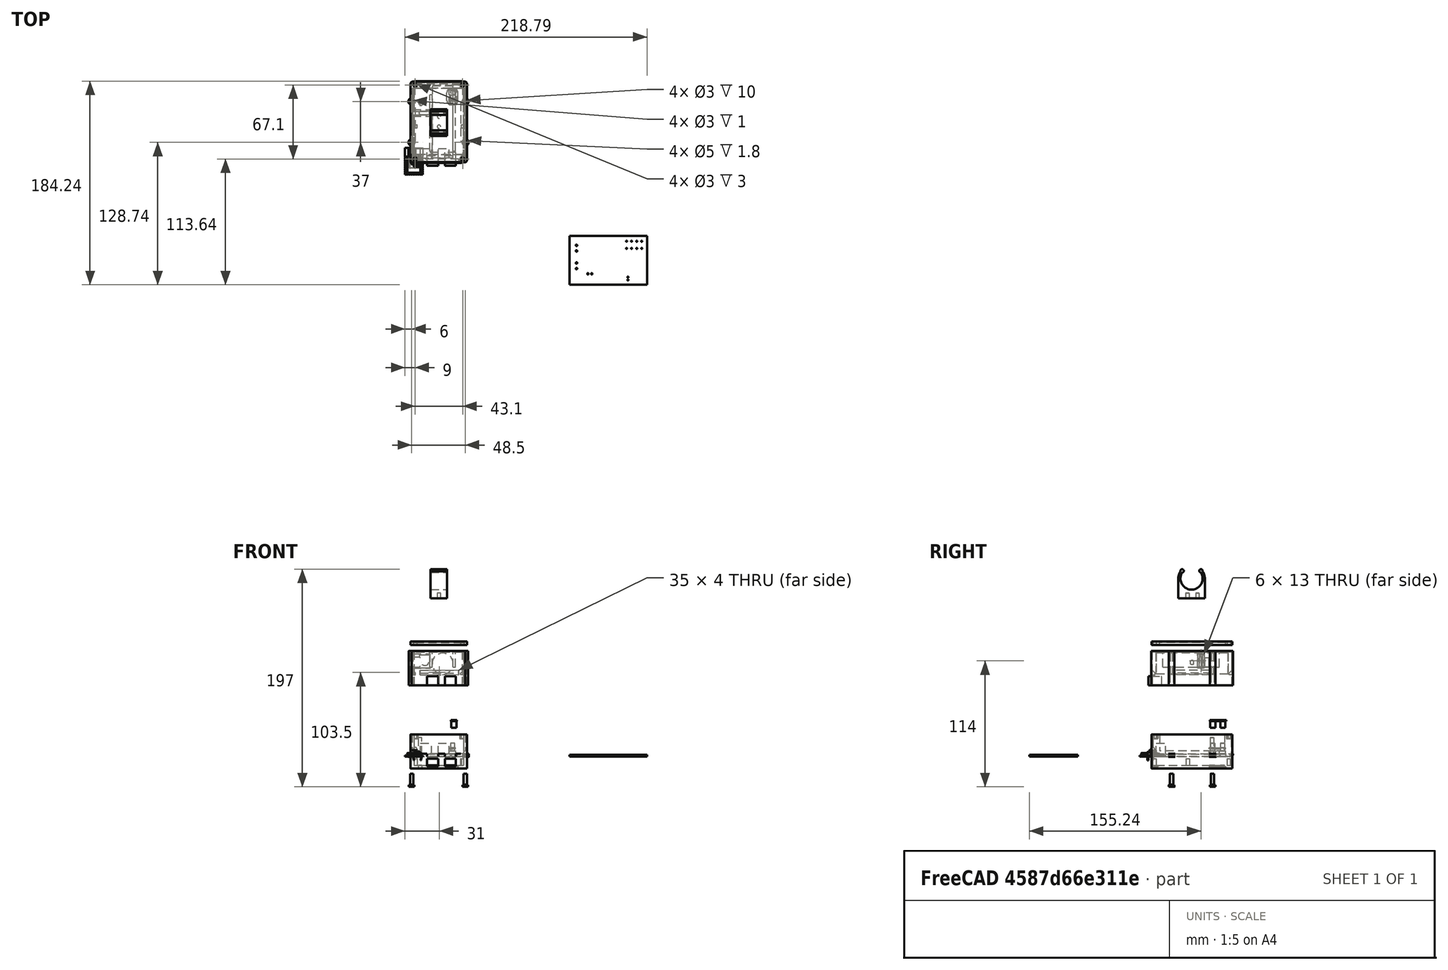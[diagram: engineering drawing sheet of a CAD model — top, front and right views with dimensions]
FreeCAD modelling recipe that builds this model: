
FCSTD DOCUMENT  (FreeCAD 0.20R29603 (Git))
Label: box_uchet_plus
License: All rights reserved
LicenseURL: http://en.wikipedia.org/wiki/All_rights_reserved
objects: Part::Box×68, Part::Cylinder×55, Part::MultiFuse×44, Part::Cut×40, Part::Feature×37, App::Part×37, Part::Fillet×31, Part::FeaturePython×16, Part::Chamfer×6, Part::Part2DObjectPython×5, Part::Extrusion×2, Part::MultiCommon×1, Part::Mirroring×1
note: 306 computed .brp shape members not serialized (recipe doc carries the construction recipe); baked Part::Feature solids carry a one-line shape summary decoded from their .brp

FEATURE [Part::Box] Box  label="Куб"
  AttacherType = Attacher::AttachEngine3D
  Height = 2
  Length = 45
  Width = 70
FEATURE [Part::Box] Box001  label="Куб001"
  AttacherType = Attacher::AttachEngine3D
  Height = 10
  Length = 10
  Placement = pos=(6,3,2) rot=(0,0,1;0rad)
  Width = 8.5
FEATURE [Part::Box] Box002  label="Куб002"
  AttacherType = Attacher::AttachEngine3D
  Height = 10
  Length = 10
  Placement = pos=(22,3,2) rot=(0,0,1;0rad)
  Width = 8.5
FEATURE [Part::Cylinder] Cylinder  label="Цилиндр"
  Angle = 360
  AttacherType = Attacher::AttachEngine3D
  FirstAngle = 0
  Height = 17
  Placement = pos=(5.5,53.5,0) rot=(0,0,1;0rad)
  Radius = 1.5
  SecondAngle = 0
FEATURE [Part::Box] Box003  label="Куб003"
  AttacherType = Attacher::AttachEngine3D
  Height = 3
  Length = 6
  Width = 6
FEATURE [Part::Cylinder] Cylinder001  label="Цилиндр001"
  Angle = 360
  AttacherType = Attacher::AttachEngine3D
  FirstAngle = 0
  Height = 10
  Placement = pos=(3,3,0) rot=(0,0,1;0rad)
  Radius = 2
  SecondAngle = 0
FEATURE [Part::MultiFuse] Fusion
  Placement = pos=(32,60,2) rot=(0,0,1;0rad)
  Shapes = -> [Cylinder001,Box003]
FEATURE [Part::Box] Box004  label="Куб004"
  AttacherType = Attacher::AttachEngine3D
  Height = 3
  Length = 6
  Width = 6
FEATURE [Part::Cylinder] Cylinder002  label="Цилиндр002"
  Angle = 360
  AttacherType = Attacher::AttachEngine3D
  FirstAngle = 0
  Height = 10
  Placement = pos=(3,3,0) rot=(0,0,1;0rad)
  Radius = 2
  SecondAngle = 0
FEATURE [Part::MultiFuse] Fusion001
  Placement = pos=(32,51,2) rot=(0,0,1;0rad)
  Shapes = -> [Cylinder002,Box004]
FEATURE [Part::Box] Box005  label="Куб005"
  AttacherType = Attacher::AttachEngine3D
  Height = 12
  Length = 45
  Placement = pos=(0,0,-4) rot=(0,0,1;0rad)
  Width = 70
FEATURE [Part::MultiFuse] Fusion002
  Shapes = -> [Fusion001,Fusion,Cylinder,Box002,Box001,Box]
FEATURE [Part::Box] Box006  label="Куб006"
  AttacherType = Attacher::AttachEngine3D
  Height = 16
  Length = 48
  Placement = pos=(-1.5,6,-21) rot=(0,0,1;0rad)
  Width = 59
FEATURE [Part::Box] Box007  label="Куб007"
  AttacherType = Attacher::AttachEngine3D
  Height = 15
  Length = 51
  Placement = pos=(-3,-1,-4) rot=(0,0,1;0rad)
  Width = 72
FEATURE [Part::Cut] Cut
  Base = -> Box007
  Tool = -> Box005
FEATURE [Part::Fillet] Fillet
  Base = -> Cut
  Edges = 1 edges r=2: [Edge11]
FEATURE [Part::Fillet] Fillet001
  Base = -> Fillet
  Edges = 1 edges r=2: [Edge13]
FEATURE [Part::Fillet] Fillet002
  Base = -> Fillet001
  Edges = 1 edges r=2: [Edge8]
FEATURE [Part::Fillet] Fillet003
  Base = -> Fillet002
  Edges = 1 edges r=2: [Edge16]
FEATURE [Part::Box] Box008  label="Куб008"
  AttacherType = Attacher::AttachEngine3D
  Height = 2
  Length = 45
  Width = 70
FEATURE [Part::Box] Box009  label="Куб009"
  AttacherType = Attacher::AttachEngine3D
  Height = 10
  Length = 10
  Placement = pos=(6,3,2) rot=(0,0,1;0rad)
  Width = 8.5
FEATURE [Part::Box] Box010  label="Куб010"
  AttacherType = Attacher::AttachEngine3D
  Height = 10
  Length = 10
  Placement = pos=(22,3,2) rot=(0,0,1;0rad)
  Width = 8.5
FEATURE [Part::Box] Box011  label="Куб011"
  AttacherType = Attacher::AttachEngine3D
  Height = 3
  Length = 6
  Width = 6
FEATURE [Part::Box] Box012  label="Куб012"
  AttacherType = Attacher::AttachEngine3D
  Height = 3
  Length = 6
  Width = 6
FEATURE [Part::Cylinder] Cylinder003  label="Цилиндр003"
  Angle = 360
  AttacherType = Attacher::AttachEngine3D
  FirstAngle = 0
  Height = 17
  Placement = pos=(5.5,53.5,0) rot=(0,0,1;0rad)
  Radius = 1.5
  SecondAngle = 0
FEATURE [Part::Cylinder] Cylinder004  label="Цилиндр004"
  Angle = 360
  AttacherType = Attacher::AttachEngine3D
  FirstAngle = 0
  Height = 10
  Placement = pos=(3,3,0) rot=(0,0,1;0rad)
  Radius = 2
  SecondAngle = 0
FEATURE [Part::Cylinder] Cylinder005  label="Цилиндр005"
  Angle = 360
  AttacherType = Attacher::AttachEngine3D
  FirstAngle = 0
  Height = 10
  Placement = pos=(3,3,0) rot=(0,0,1;0rad)
  Radius = 2
  SecondAngle = 0
FEATURE [Part::MultiFuse] Fusion003
  Placement = pos=(32,60,2) rot=(0,0,1;0rad)
  Shapes = -> [Cylinder004,Box011]
FEATURE [Part::MultiFuse] Fusion004
  Placement = pos=(32,51,2) rot=(0,0,1;0rad)
  Shapes = -> [Cylinder005,Box012]
FEATURE [Part::MultiFuse] Fusion005
  Shapes = -> [Fusion004,Fusion003,Cylinder003,Box010,Box009,Box008]
FEATURE [Part::Cut] Cut001
  Base = -> Fillet003
  Tool = -> Fusion002
FEATURE [Part::Box] Box013  label="Куб013"
  AttacherType = Attacher::AttachEngine3D
  Height = 7
  Length = 10
  Placement = pos=(6,-4,2) rot=(0,0,1;0rad)
  Width = 9
FEATURE [Part::Box] Box014  label="Куб014"
  AttacherType = Attacher::AttachEngine3D
  Height = 7
  Length = 10
  Placement = pos=(22,-3,2) rot=(0,0,1;0rad)
  Width = 8
FEATURE [Part::Cut] Cut002
  Base = -> Cut001
  Tool = -> Box013
FEATURE [Part::Cut] Cut003
  Base = -> Cut002
  Tool = -> Box014
FEATURE [Part::Box] Box015  label="Куб015"
  AttacherType = Attacher::AttachEngine3D
  Height = 10
  Length = 19
  Placement = pos=(30,49,9.5) rot=(0,0,1;0rad)
  Width = 19
FEATURE [Part::Fillet] Fillet004
  Base = -> Box015
  Edges = 2 edges r=3: [Edge1,Edge3]
FEATURE [Part::Cut] Cut004
  Base = -> Cut003
  Tool = -> Fillet004
FEATURE [Part::Fillet] Fillet005
  Base = -> Cut004
  Edges = 1 edges r=3: [Edge29]
FEATURE [Part::Fillet] Fillet006
  Base = -> Fillet005
  Edges = 1 edges r=0.5: [Edge35]
FEATURE [Part::Box] Box016  label="Куб016"
  AttacherType = Attacher::AttachEngine3D
  Height = 9
  Length = 3
  Placement = pos=(0,0,2) rot=(0,0,1;0rad)
  Width = 3
FEATURE [Part::Box] Box017  label="Куб017"
  AttacherType = Attacher::AttachEngine3D
  Height = 9
  Length = 3
  Placement = pos=(0,30,2) rot=(0,0,1;0rad)
  Width = 3
FEATURE [Part::Box] Box018  label="Куб018"
  AttacherType = Attacher::AttachEngine3D
  Height = 9
  Length = 3
  Placement = pos=(0,67,2) rot=(0,0,1;0rad)
  Width = 3
FEATURE [Part::Box] Box019  label="Куб019"
  AttacherType = Attacher::AttachEngine3D
  Height = 9
  Length = 3
  Placement = pos=(27,57,2) rot=(0,0,1;0rad)
  Width = 3
FEATURE [Part::Box] Box020  label="Куб020"
  AttacherType = Attacher::AttachEngine3D
  Height = 9
  Length = 3
  Placement = pos=(45,31,2) rot=(0,0,1;0rad)
  Width = 3
FEATURE [Part::Box] Box021  label="Куб021"
  AttacherType = Attacher::AttachEngine3D
  Height = 9
  Length = 3
  Placement = pos=(42,0,2) rot=(0,0,1;0rad)
  Width = 3
FEATURE [Part::Box] Box022  label="Куб022"
  AttacherType = Attacher::AttachEngine3D
  Height = 7
  Length = 3
  Placement = pos=(42,67,2) rot=(0,0,1;0rad)
  Width = 3
FEATURE [Part::MultiFuse] Fusion006
  Shapes = -> [Box021,Box022,Box020,Box018,Box019,Box017,Box016,Fillet006]
FEATURE [Part::Box] Box025  label="Куб025"
  AttacherType = Attacher::AttachEngine3D
  Height = 16
  Length = 45
  Placement = pos=(0,0,-20) rot=(0,0,1;0rad)
  Width = 71
FEATURE [Part::Box] Box026  label="Куб026"
  AttacherType = Attacher::AttachEngine3D
  Height = 16
  Length = 51
  Placement = pos=(-3,-1,-20) rot=(0,0,1;0rad)
  Width = 73
FEATURE [Part::Cut] Cut005
  Base = -> Box026
  Tool = -> Box025
FEATURE [Part::Fillet] Fillet007
  Base = -> Cut005
  Edges = 4 edges r=2: [Edge1,Edge3,Edge6,Edge15]
FEATURE [Part::Cut] Cut006
  Base = -> Fillet007
  Tool = -> Box006
FEATURE [Part::MultiFuse] Fusion007
  Shapes = -> [Cut006,Fusion006]
FEATURE [Part::FeaturePython] Tube  # WARN: FeaturePython — macro-defined, semantics opaque (R4)
  AttacherType = Attacher::AttachEngine3D
  Height = 4
  InnerRadius = 1.4
  OuterRadius = 2.5
  Placement = pos=(1,2,-20) rot=(0,0,1;0rad)
FEATURE [Part::FeaturePython] Tube001  # WARN: FeaturePython — macro-defined, semantics opaque (R4)
  AttacherType = Attacher::AttachEngine3D
  Height = 4
  InnerRadius = 1.4
  OuterRadius = 2.5
  Placement = pos=(44,2,-20) rot=(0,0,1;0rad)
FEATURE [Part::FeaturePython] Tube002  # WARN: FeaturePython — macro-defined, semantics opaque (R4)
  AttacherType = Attacher::AttachEngine3D
  Height = 4
  InnerRadius = 1.4
  OuterRadius = 2.5
  Placement = pos=(44.1,69.1,-20) rot=(0,0,1;0rad)
FEATURE [Part::FeaturePython] Tube003  # WARN: FeaturePython — macro-defined, semantics opaque (R4)
  AttacherType = Attacher::AttachEngine3D
  Height = 4
  InnerRadius = 1.4
  OuterRadius = 2.5
  Placement = pos=(1.1,69.1,-20) rot=(0,0,1;0rad)
FEATURE [Part::MultiFuse] Fusion008
  Shapes = -> [Fusion007,Tube,Tube001,Tube002,Tube003]
FEATURE [Part::Part2DObjectPython] ShapeString  # Draft 2D object (typed FeaturePython)
  FontFile = <userpath>/Downloads/Roboto/Roboto-Bold.ttf
  MakeFace = true
  Placement = pos=(-54.85,40.61,0) rot=(0,0,1;0rad)
  Size = 8
  String = 1
  Tracking = 0
FEATURE [Part::Part2DObjectPython] ShapeString001  # Draft 2D object (typed FeaturePython)
  FontFile = <userpath>/Downloads/Roboto/Roboto-Bold.ttf
  MakeFace = true
  Placement = pos=(-54.85,40.61,0) rot=(0,0,1;0rad)
  Size = 8
  String = 2
  Tracking = 0
FEATURE [Part::Extrusion] Extrude001
  Base = -> ShapeString001
  Dir = (0,0,1)
  DirMode = 2
  FaceMakerClass = Part::FaceMakerBullseye
  LengthFwd = 5
  LengthRev = 0
  Placement = pos=(55,69,9) rot=(0,0,1;1.5708rad)
  Solid = false
  Symmetric = false
FEATURE [Part::Part2DObjectPython] ShapeString002  # Draft 2D object (typed FeaturePython)
  FontFile = <userpath>/Downloads/Roboto/Roboto-Bold.ttf
  MakeFace = true
  Placement = pos=(-54.85,40.61,0) rot=(0,0,1;0rad)
  Size = 8
  String = 1
  Tracking = 0
FEATURE [Part::Extrusion] Extrude002
  Base = -> ShapeString002
  Dir = (0,0,1)
  DirMode = 2
  FaceMakerClass = Part::FaceMakerBullseye
  LengthFwd = 5
  LengthRev = 0
  Placement = pos=(71,69,9) rot=(0,0,1;1.5708rad)
  Solid = false
  Symmetric = false
FEATURE [Part::Cut] Cut007
  Base = -> Fusion008
  Tool = -> Extrude001
FEATURE [Part::Cut] Cut008
  Base = -> Cut007
  Tool = -> Extrude002
FEATURE [Part::Box] Box027  label="Куб027"
  AttacherType = Attacher::AttachEngine3D
  Height = 3
  Length = 51
  Placement = pos=(-3,-1,-23) rot=(0,0,1;0rad)
  Width = 73
FEATURE [Part::Fillet] Fillet008
  Base = -> Box027
  Edges = 4 edges r=2: [Edge1,Edge3,Edge5,Edge7]
FEATURE [Part::Box] Box028  label="Куб028"
  AttacherType = Attacher::AttachEngine3D
  Height = 2
  Length = 45
  Width = 70
FEATURE [Part::Box] Box031  label="Куб031"
  AttacherType = Attacher::AttachEngine3D
  Height = 3
  Length = 6
  Width = 6
FEATURE [Part::Box] Box032  label="Куб032"
  AttacherType = Attacher::AttachEngine3D
  Height = 3
  Length = 6
  Width = 6
FEATURE [Part::Box] Box033  label="Куб033"
  AttacherType = Attacher::AttachEngine3D
  Height = 12
  Length = 45
  Placement = pos=(0,0,-4) rot=(0,0,1;0rad)
  Width = 71
FEATURE [Part::Box] Box034  label="Куб034"
  AttacherType = Attacher::AttachEngine3D
  Height = 16
  Length = 48
  Placement = pos=(-1.5,6,-21) rot=(0,0,1;0rad)
  Width = 59
FEATURE [Part::Box] Box035  label="Куб035"
  AttacherType = Attacher::AttachEngine3D
  Height = 15
  Length = 51
  Placement = pos=(-3,-1,-4) rot=(0,0,1;0rad)
  Width = 73
FEATURE [Part::Box] Box037  label="Куб037"
  AttacherType = Attacher::AttachEngine3D
  Height = 7
  Length = 10
  Placement = pos=(28,-3,2) rot=(0,0,1;0rad)
  Width = 8
FEATURE [Part::Box] Box039  label="Куб039"
  AttacherType = Attacher::AttachEngine3D
  Height = 6
  Length = 3
  Placement = pos=(0,0,2) rot=(0,0,1;0rad)
  Width = 3
FEATURE [Part::Box] Box040  label="Куб040"
  AttacherType = Attacher::AttachEngine3D
  Height = 6
  Length = 3
  Placement = pos=(0,30,2) rot=(0,0,1;0rad)
  Width = 3
FEATURE [Part::Box] Box041  label="Куб041"
  AttacherType = Attacher::AttachEngine3D
  Height = 6
  Length = 3
  Placement = pos=(0,67,2) rot=(0,0,1;0rad)
  Width = 3
FEATURE [Part::Box] Box043  label="Куб043"
  AttacherType = Attacher::AttachEngine3D
  Height = 6
  Length = 3
  Placement = pos=(43,30,2) rot=(0,0,1;0rad)
  Width = 3
FEATURE [Part::Box] Box044  label="Куб044"
  AttacherType = Attacher::AttachEngine3D
  Height = 6
  Length = 3
  Placement = pos=(42,0,2) rot=(0,0,1;0rad)
  Width = 3
FEATURE [Part::Box] Box045  label="Куб045"
  AttacherType = Attacher::AttachEngine3D
  Height = 6
  Length = 3
  Placement = pos=(42,67,2) rot=(0,0,1;0rad)
  Width = 3
FEATURE [Part::Box] Box046  label="Куб046"
  AttacherType = Attacher::AttachEngine3D
  Height = 16
  Length = 45
  Placement = pos=(0,0,-20) rot=(0,0,1;0rad)
  Width = 71
FEATURE [Part::Box] Box047  label="Куб047"
  AttacherType = Attacher::AttachEngine3D
  Height = 16
  Length = 51
  Placement = pos=(-3,-1,-20) rot=(0,0,1;0rad)
  Width = 73
FEATURE [Part::Cut] Cut009
  Base = -> Box035
  Tool = -> Box033
FEATURE [Part::Cut] Cut014
  Base = -> Box047
  Tool = -> Box046
FEATURE [Part::Cylinder] Cylinder006  label="Цилиндр006"
  Angle = 360
  AttacherType = Attacher::AttachEngine3D
  FirstAngle = 0
  Height = 17
  Placement = pos=(5.7,52.7,0) rot=(0,0,1;0rad)
  Radius = 1.5
  SecondAngle = 0
FEATURE [Part::Cylinder] Cylinder007  label="Цилиндр007"
  Angle = 360
  AttacherType = Attacher::AttachEngine3D
  FirstAngle = 0
  Height = 10
  Placement = pos=(3,3,0) rot=(0,0,1;0rad)
  Radius = 2
  SecondAngle = 0
FEATURE [Part::Cylinder] Cylinder008  label="Цилиндр008"
  Angle = 360
  AttacherType = Attacher::AttachEngine3D
  FirstAngle = 0
  Height = 10
  Placement = pos=(3,3,0) rot=(0,0,1;0rad)
  Radius = 2
  SecondAngle = 0
FEATURE [Part::Fillet] Fillet009
  Base = -> Cut009
  Edges = 1 edges r=2: [Edge11]
FEATURE [Part::Fillet] Fillet010
  Base = -> Fillet009
  Edges = 1 edges r=2: [Edge13]
FEATURE [Part::Fillet] Fillet011
  Base = -> Fillet010
  Edges = 1 edges r=2: [Edge8]
FEATURE [Part::Fillet] Fillet012
  Base = -> Fillet011
  Edges = 1 edges r=2: [Edge16]
FEATURE [Part::Fillet] Fillet016
  Base = -> Cut014
  Edges = 4 edges r=2: [Edge1,Edge3,Edge6,Edge15]
FEATURE [Part::Cut] Cut015
  Base = -> Fillet016
  Tool = -> Box034
FEATURE [Part::MultiFuse] Fusion009
  Placement = pos=(32,60,2) rot=(0,0,1;0rad)
  Shapes = -> [Cylinder007,Box031]
FEATURE [Part::MultiFuse] Fusion010
  Placement = pos=(32,51,2) rot=(0,0,1;0rad)
  Shapes = -> [Cylinder008,Box032]
FEATURE [Part::MultiFuse] Fusion011
  Shapes = -> [Fusion010,Fusion009,Cylinder006,Box028]
FEATURE [Part::Cut] Cut010
  Base = -> Fillet012
  Tool = -> Fusion011
FEATURE [Part::MultiFuse] Fusion012
  Shapes = -> [Box044,Box045,Box043,Box041,Box040,Box039]
FEATURE [Part::MultiFuse] Fusion013
  Shapes = -> [Cut015,Fusion012]
FEATURE [Part::Part2DObjectPython] ShapeString003  # Draft 2D object (typed FeaturePython)
  FontFile = <userpath>/Downloads/Roboto/Roboto-Bold.ttf
  MakeFace = true
  Placement = pos=(-54.85,40.61,0) rot=(0,0,1;0rad)
  Size = 8
  String = 2
  Tracking = 0
FEATURE [Part::Part2DObjectPython] ShapeString004  # Draft 2D object (typed FeaturePython)
  FontFile = <userpath>/Downloads/Roboto/Roboto-Bold.ttf
  MakeFace = true
  Placement = pos=(-54.85,40.61,0) rot=(0,0,1;0rad)
  Size = 8
  String = 1
  Tracking = 0
FEATURE [Part::FeaturePython] Tube004  # WARN: FeaturePython — macro-defined, semantics opaque (R4)
  AttacherType = Attacher::AttachEngine3D
  Height = 4
  InnerRadius = 1.4
  OuterRadius = 2.5
  Placement = pos=(1,2,-20) rot=(0,0,1;0rad)
FEATURE [Part::FeaturePython] Tube005  # WARN: FeaturePython — macro-defined, semantics opaque (R4)
  AttacherType = Attacher::AttachEngine3D
  Height = 4
  InnerRadius = 1.4
  OuterRadius = 2.5
  Placement = pos=(44,2,-20) rot=(0,0,1;0rad)
FEATURE [Part::FeaturePython] Tube006  # WARN: FeaturePython — macro-defined, semantics opaque (R4)
  AttacherType = Attacher::AttachEngine3D
  Height = 4
  InnerRadius = 1.4
  OuterRadius = 2.5
  Placement = pos=(44,69,-20) rot=(0,0,1;0rad)
FEATURE [Part::FeaturePython] Tube007  # WARN: FeaturePython — macro-defined, semantics opaque (R4)
  AttacherType = Attacher::AttachEngine3D
  Height = 4
  InnerRadius = 1.4
  OuterRadius = 2.5
  Placement = pos=(1,69,-20) rot=(0,0,1;0rad)
FEATURE [Part::Cut] Cut018
  Base = -> Fillet008
  Tool = -> Cut008
FEATURE [Part::Cylinder] Cylinder009  label="Цилиндр009"
  Angle = 360
  AttacherType = Attacher::AttachEngine3D
  FirstAngle = 0
  Height = 10
  Placement = pos=(1,2,-24) rot=(0,0,1;0rad)
  Radius = 1.5
  SecondAngle = 0
FEATURE [Part::Cylinder] Cylinder010  label="Цилиндр010"
  Angle = 360
  AttacherType = Attacher::AttachEngine3D
  FirstAngle = 0
  Height = 10
  Placement = pos=(1.1,69.1,-26) rot=(0,0,1;0rad)
  Radius = 1.5
  SecondAngle = 0
FEATURE [Part::Cylinder] Cylinder011  label="Цилиндр011"
  Angle = 360
  AttacherType = Attacher::AttachEngine3D
  FirstAngle = 0
  Height = 10
  Placement = pos=(44.1,69.1,-26) rot=(0,0,1;0rad)
  Radius = 1.5
  SecondAngle = 0
FEATURE [Part::Cylinder] Cylinder012  label="Цилиндр012"
  Angle = 360
  AttacherType = Attacher::AttachEngine3D
  FirstAngle = 0
  Height = 10
  Placement = pos=(44,2,-24) rot=(0,0,1;0rad)
  Radius = 1.5
  SecondAngle = 0
FEATURE [Part::Cut] Cut019
  Base = -> Cut018
  Tool = -> Cylinder009
FEATURE [Part::Cut] Cut020
  Base = -> Cut019
  Tool = -> Cylinder012
FEATURE [Part::Cut] Cut021
  Base = -> Cut020
  Tool = -> Cylinder011
FEATURE [Part::Cut] Cut022
  Base = -> Cut021
  Tool = -> Cylinder010
FEATURE [Part::Cylinder] Cylinder013  label="Цилиндр013"
  Angle = 360
  AttacherType = Attacher::AttachEngine3D
  FirstAngle = 0
  Height = 15
  Radius = 10
  SecondAngle = 0
FEATURE [Part::Box] Box048  label="Куб048"
  AttacherType = Attacher::AttachEngine3D
  Height = 15
  Length = 24
  Placement = pos=(-12,-7,0) rot=(0,0,1;0rad)
  Width = 25
FEATURE [Part::Cut] Cut023
  Base = -> Box048
  Tool = -> Cylinder013
FEATURE [Part::Cylinder] Cylinder014  label="Цилиндр014"
  Angle = 360
  AttacherType = Attacher::AttachEngine3D
  FirstAngle = 0
  Height = 15
  Radius = 12
  SecondAngle = 0
FEATURE [Part::Box] Box049  label="Куб049"
  AttacherType = Attacher::AttachEngine3D
  Height = 15
  Length = 24
  Placement = pos=(-12,0,0) rot=(0,0,1;0rad)
  Width = 18
FEATURE [Part::Cylinder] Cylinder015  label="Цилиндр015"
  Angle = 360
  AttacherType = Attacher::AttachEngine3D
  FirstAngle = 0
  Height = 15
  Radius = 10
  SecondAngle = 0
FEATURE [Part::Cut] Cut024
  Base = -> Box049
  Tool = -> Cylinder015
FEATURE [Part::MultiCommon] Common
  Shapes = -> [Cut023,Cylinder014]
FEATURE [Part::Cylinder] Cylinder016  label="Цилиндр016"
  Angle = 360
  AttacherType = Attacher::AttachEngine3D
  FirstAngle = 0
  Height = 15
  Placement = pos=(-8.5,-7,0) rot=(0,0,1;0rad)
  Radius = 1.5
  SecondAngle = 0
FEATURE [Part::Cylinder] Cylinder017  label="Цилиндр017"
  Angle = 360
  AttacherType = Attacher::AttachEngine3D
  FirstAngle = 0
  Height = 15
  Placement = pos=(8.5,-7,0) rot=(0,0,1;0rad)
  Radius = 1.5
  SecondAngle = 0
FEATURE [Part::MultiFuse] Fusion015
  Placement = pos=(30,35,113) rot=(0.57735,0.57735,-0.57735;4.18879rad)
  Shapes = -> [Cut024,Common,Cylinder016,Cylinder017]
FEATURE [Part::Box] Box050  label="Куб050"
  AttacherType = Attacher::AttachEngine3D
  Height = 16
  Length = 48
  Placement = pos=(-1.5,6,-21) rot=(0,0,1;0rad)
  Width = 60
FEATURE [Part::Fillet] Fillet017
  Base = -> Box050
  Edges = 2 edges r=3: [Edge4,Edge8]
  Placement = pos=(0,-1,-1) rot=(0,0,1;0rad)
FEATURE [Part::Cylinder] Cylinder018  label="Цилиндр018"
  Angle = 360
  AttacherType = Attacher::AttachEngine3D
  FirstAngle = 0
  Height = 4
  Placement = pos=(35,63,7) rot=(0,0,1;0rad)
  Radius = 1.8
  SecondAngle = 0
FEATURE [Part::Cylinder] Cylinder019  label="Цилиндр019"
  Angle = 360
  AttacherType = Attacher::AttachEngine3D
  FirstAngle = 0
  Height = 4
  Placement = pos=(35,54,7) rot=(0,0,1;0rad)
  Radius = 1.8
  SecondAngle = 0
FEATURE [Part::Box] Box051  label="Куб051"
  AttacherType = Attacher::AttachEngine3D
  Height = 1
  Length = 5
  Placement = pos=(32.5,51,6) rot=(0,0,1;0rad)
  Width = 15
FEATURE [Part::Fillet] Fillet018
  Base = -> Box051
  Edges = 4 edges r=2: [Edge1,Edge3,Edge5,Edge7]
FEATURE [Part::MultiFuse] Fusion017
  Placement = pos=(0,0,1) rot=(0,0,1;0rad)
  Shapes = -> [Cylinder018,Cylinder019,Fillet018]
FEATURE [Part::Cut] Cut026
  Base = -> Cut022
  Placement = pos=(0,71,81) rot=(1,0,0;3.14159rad)
  Tool = -> Fillet017
FEATURE [Part::Box] Box036  label="Куб036"
  AttacherType = Attacher::AttachEngine3D
  Height = 7
  Length = 10
  Placement = pos=(12,-4,2) rot=(0,0,1;0rad)
  Width = 9
FEATURE [Part::Cut] Cut027
  Base = -> Cut010
  Tool = -> Box037
FEATURE [Part::Cut] Cut028
  Base = -> Cut027
  Tool = -> Box036
FEATURE [Part::Box] Box052  label="Куб052"
  AttacherType = Attacher::AttachEngine3D
  Height = 10
  Length = 10
  Placement = pos=(29.8,51,9) rot=(0,0,1;0rad)
  Width = 15
FEATURE [Part::Fillet] Fillet019
  Base = -> Box052
  Edges = 4 edges r=4: [Edge1,Edge3,Edge5,Edge7]
FEATURE [Part::Cut] Cut029
  Base = -> Cut028
  Tool = -> Fillet019
FEATURE [Part::MultiFuse] Fusion018
  Shapes = -> [Fusion013,Tube004,Tube005,Tube006,Tube007]
FEATURE [Part::MultiFuse] Fusion019
  Shapes = -> [Fusion018,Cut029]
FEATURE [Part::Mirroring] Part__Mirroring  label="Fusion019 (Mirror #1)"
  Base = (0,0,0)
  Normal = (0,0,1)
  Source = -> Fusion019
FEATURE [Part::Cylinder] Cylinder020  label="Цилиндр020"
  Angle = 360
  AttacherType = Attacher::AttachEngine3D
  FirstAngle = 0
  Height = 65
  Placement = pos=(26,3,84) rot=(-1,0,0;1.5708rad)
  Radius = 9.5
  SecondAngle = 0
FEATURE [Part::Box] Box053  label="Куб053"
  AttacherType = Attacher::AttachEngine3D
  Height = 8
  Length = 10
  Placement = pos=(12,-4,64.5) rot=(0,0,1;0rad)
  Width = 12
FEATURE [Part::Box] Box054  label="Куб054"
  AttacherType = Attacher::AttachEngine3D
  Height = 8
  Length = 10
  Placement = pos=(28,-4,64.5) rot=(0,0,1;0rad)
  Width = 12
FEATURE [Part::Box] Box055  label="Куб055"
  AttacherType = Attacher::AttachEngine3D
  Height = 30
  Length = 46.5
  Placement = pos=(-1,-0.5,64.5) rot=(0,0,1;0rad)
  Width = 72
FEATURE [Part::Box] Box056  label="Куб056"
  AttacherType = Attacher::AttachEngine3D
  Height = 31
  Length = 48.5
  Placement = pos=(-2,-1.5,64.5) rot=(0,0,1;0rad)
  Width = 74
FEATURE [Part::Cut] Cut030
  Base = -> Box056
  Tool = -> Box055
FEATURE [Part::Fillet] Fillet020
  Base = -> Cut030
  Edges = 1 edges r=3: [Edge17]
FEATURE [Part::Fillet] Fillet021
  Base = -> Fillet020
  Edges = 1 edges r=3: [Edge18]
FEATURE [Part::Fillet] Fillet022
  Base = -> Fillet021
  Edges = 1 edges r=3: [Edge17]
FEATURE [Part::Fillet] Fillet023
  Base = -> Fillet022
  Edges = 1 edges r=3: [Edge20]
FEATURE [Part::Fillet] Fillet024
  Base = -> Fillet023
  Edges = 1 edges r=4: [Edge29]
FEATURE [Part::Fillet] Fillet025
  Base = -> Fillet024
  Edges = 1 edges r=4: [Edge16]
FEATURE [Part::Fillet] Fillet026
  Base = -> Fillet025
  Edges = 1 edges r=4: [Edge23]
FEATURE [Part::Fillet] Fillet027
  Base = -> Fillet026
  Edges = 1 edges r=4: [Edge17]
FEATURE [Part::Box] Box057  label="Куб057"
  AttacherType = Attacher::AttachEngine3D
  Height = 8
  Length = 10
  Placement = pos=(12,-4,64.5) rot=(0,0,1;0rad)
  Width = 12
FEATURE [Part::Box] Box058  label="Куб058"
  AttacherType = Attacher::AttachEngine3D
  Height = 8
  Length = 10
  Placement = pos=(28,-4,64.5) rot=(0,0,1;0rad)
  Width = 12
FEATURE [Part::Cut] Cut031
  Base = -> Fillet027
  Tool = -> Box057
FEATURE [Part::Cut] Cut032
  Base = -> Cut031
  Tool = -> Box058
FEATURE [Part::Box] Box059  label="Куб059"
  AttacherType = Attacher::AttachEngine3D
  Height = 4
  Length = 3
  Width = 35
FEATURE [Part::Chamfer] Chamfer
  Base = -> Box059
  Edges = 1 edges r=2.5: [Edge6]
  Placement = pos=(-1.5,18,74) rot=(0,0,1;0rad)
FEATURE [Part::Box] Box060  label="Куб060"
  AttacherType = Attacher::AttachEngine3D
  Height = 4
  Length = 3
  Width = 35
FEATURE [Part::Chamfer] Chamfer001
  Base = -> Box060
  Edges = 1 edges r=2.5: [Edge6]
  Placement = pos=(45.5,53,74) rot=(0,0,1;3.14159rad)
FEATURE [Part::Box] Box061  label="Куб061"
  AttacherType = Attacher::AttachEngine3D
  Height = 4
  Length = 3
  Width = 35
FEATURE [Part::Chamfer] Chamfer002
  Base = -> Box061
  Edges = 1 edges r=2.5: [Edge6]
  Placement = pos=(40.5,-1,74) rot=(0,0,1;1.5708rad)
FEATURE [Part::Box] Box062  label="Куб062"
  AttacherType = Attacher::AttachEngine3D
  Height = 4
  Length = 3
  Width = 35
FEATURE [Part::Chamfer] Chamfer003
  Base = -> Box062
  Edges = 1 edges r=2.5: [Edge6]
  Placement = pos=(5.5,72,74) rot=(0,0,-1;1.5708rad)
FEATURE [Part::Box] Box063  label="Куб063"
  AttacherType = Attacher::AttachEngine3D
  Height = 2.5
  Length = 48.5
  Placement = pos=(-2,-1.5,62) rot=(0,0,1;0rad)
  Width = 74
FEATURE [Part::Fillet] Fillet028
  Base = -> Box063
  Edges = 4 edges r=4: [Edge1,Edge3,Edge5,Edge7]
FEATURE [Part::Cylinder] Cylinder021  label="Цилиндр021"
  Angle = 360
  AttacherType = Attacher::AttachEngine3D
  FirstAngle = 0
  Height = 10
  Placement = pos=(6,53,58) rot=(0,0,1;0rad)
  Radius = 1.6
  SecondAngle = 0
FEATURE [Part::Cylinder] Cylinder022  label="Цилиндр022"
  Angle = 360
  AttacherType = Attacher::AttachEngine3D
  FirstAngle = 0
  Height = 10
  Placement = pos=(36.2,54.2,58) rot=(0,0,1;0rad)
  Radius = 2.4
  SecondAngle = 0
FEATURE [Part::Cut] Cut033
  Base = -> Fillet028
  Tool = -> Cylinder021
FEATURE [Part::Cylinder] Cylinder023  label="Цилиндр023"
  Angle = 360
  AttacherType = Attacher::AttachEngine3D
  FirstAngle = 0
  Height = 10
  Placement = pos=(36.2,63.3,58) rot=(0,0,1;0rad)
  Radius = 2.4
  SecondAngle = 0
FEATURE [Part::Cut] Cut034
  Base = -> Cut033
  Tool = -> Cylinder023
FEATURE [Part::Cut] Cut035
  Base = -> Cut034
  Tool = -> Cylinder022
FEATURE [Part::Chamfer] Chamfer004
  Base = -> Cut035
  Edges = 1 edges r=1: [Edge23]
FEATURE [Part::Fillet] Fillet029
  Base = -> Chamfer004
  Edges = 1 edges r=2: [Edge10]
FEATURE [Part::Fillet] Fillet030
  Base = -> Fillet029
  Edges = 1 edges r=2: [Edge11]
FEATURE [Part::Fillet] Fillet031
  Base = -> Fillet030
  Edges = 8 edges r=2: [Edge4,Edge5,Edge6,Edge7,Edge8,Edge9,Edge10,Edge11]
FEATURE [Part::Cylinder] Cylinder024  label="Цилиндр024"
  Angle = 360
  AttacherType = Attacher::AttachEngine3D
  FirstAngle = 0
  Height = 10
  Placement = pos=(10,66,85) rot=(-1,0,0;1.53589rad)
  Radius = 3.1
  SecondAngle = 0
FEATURE [Part::Cut] Cut036
  Base = -> Cut032
  Tool = -> Cylinder024
FEATURE [Part::Box] Box064  label="Куб064"
  AttacherType = Attacher::AttachEngine3D
  Height = 9
  Length = 18
  Width = 3
FEATURE [Part::Fillet] Fillet032
  Base = -> Box064
  Edges = 4 edges r=1: [Edge9,Edge10,Edge11,Edge12]
  Placement = pos=(5,42,92) rot=(0,1,0;1.5708rad)
FEATURE [Part::Box] Box065  label="Куб065"
  AttacherType = Attacher::AttachEngine3D
  Height = 13
  Length = 17
  Placement = pos=(-2,40.5,80) rot=(0,0,1;0rad)
  Width = 6
FEATURE [Part::MultiFuse] Fusion020
  Shapes = -> [Cut036,Box065]
FEATURE [Part::Box] Box066  label="Куб066"
  AttacherType = Attacher::AttachEngine3D
  Height = 9
  Length = 18
  Width = 3
FEATURE [Part::Fillet] Fillet033
  Base = -> Box066
  Edges = 4 edges r=1: [Edge9,Edge10,Edge11,Edge12]
  Placement = pos=(-6,42,81) rot=(0,0,1;0rad)
FEATURE [Part::Cut] Cut037
  Base = -> Fusion020
  Tool = -> Fillet033
FEATURE [Part::Cut] Cut038
  Base = -> Cut037
  Tool = -> Fillet032
FEATURE [Part::Box] Box067  label="Куб067"
  AttacherType = Attacher::AttachEngine3D
  Height = 4
  Length = 13
  Width = 3
FEATURE [Part::Chamfer] Chamfer005
  Base = -> Box067
  Edges = 4 edges r=0.6: [Edge9,Edge10,Edge11,Edge12]
  Placement = pos=(-7,34,83) rot=(0,0,1;0rad)
FEATURE [Part::Cut] Cut039
  Base = -> Cut038
  Tool = -> Chamfer005
FEATURE [Part::Box] Box068  label="Куб068"
  AttacherType = Attacher::AttachEngine3D
  Height = 14
  Length = 2
  Placement = pos=(14.5,9,81) rot=(0,0,1;0rad)
  Width = 51
FEATURE [Part::Box] Box069  label="Куб069"
  AttacherType = Attacher::AttachEngine3D
  Height = 14
  Length = 2
  Placement = pos=(35.5,9,81) rot=(0,0,1;0rad)
  Width = 51
FEATURE [Part::MultiFuse] Fusion021
  Shapes = -> [Cut039,Box068,Box069]
FEATURE [Part::Box] Box070  label="Куб070"
  AttacherType = Attacher::AttachEngine3D
  Height = 8
  Length = 10
  Placement = pos=(12,-4,64.5) rot=(0,0,1;0rad)
  Width = 12
FEATURE [Part::Box] Box071  label="Куб071"
  AttacherType = Attacher::AttachEngine3D
  Height = 8
  Length = 10
  Placement = pos=(28,-4,64.5) rot=(0,0,1;0rad)
  Width = 12
FEATURE [Part::MultiFuse] Fusion022
  Placement = pos=(0,0,-3) rot=(0,0,1;0rad)
  Shapes = -> [Box070,Box071]
FEATURE [Part::Cut] Cut040
  Base = -> Fillet031
  Tool = -> Fusion022
FEATURE [Part::Box] Box072  label="Куб072"
  AttacherType = Attacher::AttachEngine3D
  Height = 8
  Length = 6
  Placement = pos=(-3,47,81) rot=(0,0,1;0rad)
  Width = 4
FEATURE [Part::Cut] Cut041
  Base = -> Fusion021
  Tool = -> Box072
FEATURE [Part::MultiFuse] Fusion023
  Shapes = -> [Cut041,Chamfer003,Chamfer002,Chamfer001,Chamfer]
FEATURE [Part::Cylinder] Cylinder025  label="Цилиндр025"
  Angle = 360
  AttacherType = Attacher::AttachEngine3D
  FirstAngle = 0
  Height = 7
  Placement = pos=(36.2,63.3,61) rot=(0,0,1;0rad)
  Radius = 2.3
  SecondAngle = 0
FEATURE [Part::Cylinder] Cylinder026  label="Цилиндр026"
  Angle = 360
  AttacherType = Attacher::AttachEngine3D
  FirstAngle = 0
  Height = 7
  Placement = pos=(36.2,54.2,61) rot=(0,0,1;0rad)
  Radius = 2.3
  SecondAngle = 0
FEATURE [Part::Box] Box073  label="Куб073"
  AttacherType = Attacher::AttachEngine3D
  Height = 1
  Length = 5.5
  Placement = pos=(33.5,51.5,67) rot=(0,0,1;0rad)
  Width = 15
FEATURE [Part::MultiFuse] Fusion024
  Placement = pos=(0,0,-35) rot=(0,0,1;0rad)
  Shapes = -> [Box073,Cylinder026,Cylinder025]
FEATURE [Part::Feature] Part__Feature036  label="SW_PUSH_6mm004"
  shape: bbox 7.174 x 6 x 7.8 mm, 105 faces (baked)
FEATURE [App::Part] SW_PUSH_6mm002  label="SW_PUSH_6mm005"
  Group = -> [Part__Feature036]
  Origin = -> Origin036
  Placement = pos=(201.574,-78.9662,1.65) rot=(0,0,1;1.5708rad)
FEATURE [Part::Feature] Part__Feature037  label="R_0805_2012Metric034"
  shape: bbox 2 x 1.2 x 0.45 mm, 26 faces (baked)
FEATURE [App::Part] R_0805_2012Metric017  label="R_0805_2012Metric035"
  Group = -> [Part__Feature037]
  Origin = -> Origin037
  Placement = pos=(167.584,-83.2538,1.65) rot=(0,0,-1;1.5708rad)
FEATURE [Part::Feature] Part__Feature038  label="R_1206_3216Metric"
  shape: bbox 3.2 x 1.6 x 0.55 mm, 26 faces (baked)
FEATURE [App::Part] R_1206_3216Metric  label="R_1206_3216Metric001"
  Group = -> [Part__Feature038]
  Origin = -> Origin038
  Placement = pos=(171.323,-90.3625,1.65) rot=(0,0,-1;1.5708rad)
FEATURE [Part::Feature] Part__Feature039  label="R_0805_2012Metric036"
  shape: bbox 2 x 1.2 x 0.45 mm, 26 faces (baked)
FEATURE [App::Part] R_0805_2012Metric018  label="R_0805_2012Metric037"
  Group = -> [Part__Feature039]
  Origin = -> Origin039
  Placement = pos=(161.874,-73.8886,1.65) rot=(0,0,1;3.14159rad)
FEATURE [Part::Feature] Part__Feature040  label="R_0805_2012Metric038"
  shape: bbox 2 x 1.2 x 0.45 mm, 26 faces (baked)
FEATURE [App::Part] R_0805_2012Metric019  label="R_0805_2012Metric039"
  Group = -> [Part__Feature040]
  Origin = -> Origin040
  Placement = pos=(178.689,-102.387,1.65) rot=(0,0,1;1.5708rad)
FEATURE [Part::Feature] Part__Feature041  label="LED_D3.0mm_IRGrey002"
  shape: bbox 3.4 x 3.8 x 10.8 mm, 16 faces (baked)
FEATURE [App::Part] LED_D3_0mm_IRGrey001  label="LED_D3.0mm_IRGrey003"
  Group = -> [Part__Feature041]
  Origin = -> Origin041
  Placement = pos=(193.542,-107.436,1.65) rot=(0,0,1;1.5708rad)
FEATURE [Part::Feature] Part__Feature042  label="R_0805_2012Metric040"
  shape: bbox 2 x 1.2 x 0.45 mm, 26 faces (baked)
FEATURE [App::Part] R_0805_2012Metric020  label="R_0805_2012Metric041"
  Group = -> [Part__Feature042]
  Origin = -> Origin042
  Placement = pos=(181.229,-99.3375,1.65) rot=(0,0,-1;1.5708rad)
FEATURE [Part::Feature] Part__Feature043  label="C_1206_3216Metric016"
  shape: bbox 3.2 x 1.6 x 1.6 mm, 28 faces (baked)
FEATURE [App::Part] C_1206_3216Metric008  label="C_1206_3216Metric017"
  Group = -> [Part__Feature043]
  Origin = -> Origin043
  Placement = pos=(152.984,-95.1248,1.65) rot=(0,0,-1;1.5708rad)
FEATURE [Part::Feature] Part__Feature044  label="R_0805_2012Metric042"
  shape: bbox 2 x 1.2 x 0.45 mm, 26 faces (baked)
FEATURE [App::Part] R_0805_2012Metric021  label="R_0805_2012Metric043"
  Group = -> [Part__Feature044]
  Origin = -> Origin044
  Placement = pos=(182.875,-75.282,1.65) rot=(0,0,-1;1.5708rad)
FEATURE [Part::Feature] Part__Feature045  label="R_0805_2012Metric044"
  shape: bbox 2 x 1.2 x 0.45 mm, 26 faces (baked)
FEATURE [App::Part] R_0805_2012Metric022  label="R_0805_2012Metric045"
  Group = -> [Part__Feature045]
  Origin = -> Origin045
  Placement = pos=(170.69,-94.0562,1.65) rot=(0,0,1;3.14159rad)
FEATURE [Part::Feature] Part__Feature046  label="R_0805_2012Metric046"
  shape: bbox 2 x 1.2 x 0.45 mm, 26 faces (baked)
FEATURE [App::Part] R_0805_2012Metric023  label="R_0805_2012Metric047"
  Group = -> [Part__Feature046]
  Origin = -> Origin046
  Placement = pos=(182.905,-79.5039,1.65) rot=(0,0,-1;1.5708rad)
FEATURE [Part::Feature] Part__Feature047  label="R_0805_2012Metric048"
  shape: bbox 2 x 1.2 x 0.45 mm, 26 faces (baked)
FEATURE [App::Part] R_0805_2012Metric024  label="R_0805_2012Metric049"
  Group = -> [Part__Feature047]
  Origin = -> Origin047
  Placement = pos=(184.937,-73.1539,1.65) rot=(0,0,-1;1.5708rad)
FEATURE [Part::Feature] Part__Feature048  label="ESP_12E001_cp001"
  shape: bbox 16 x 24 x 3.2 mm, 488 faces, 48 solids (baked)
FEATURE [App::Part] ESP_12E001  label="ESP-12E001"
  Group = -> [Part__Feature048]
  Origin = -> Origin048
  Placement = pos=(196.138,-93.9945,1.65) rot=(0,0,-1;1.5708rad)
FEATURE [Part::Feature] Part__Feature049  label="R_0805_2012Metric050"
  shape: bbox 2 x 1.2 x 0.45 mm, 26 faces (baked)
FEATURE [App::Part] R_0805_2012Metric025  label="R_0805_2012Metric051"
  Group = -> [Part__Feature049]
  Origin = -> Origin049
  Placement = pos=(186.581,-104.642,1.65) rot=(0,0,1;3.14159rad)
FEATURE [Part::Feature] Part__Feature050  label="L_1210_3225Metric002"
  shape: bbox 3.2 x 2.5 x 2.5 mm, 28 faces (baked)
FEATURE [App::Part] L_1210_3225Metric001  label="L_1210_3225Metric003"
  Group = -> [Part__Feature050]
  Origin = -> Origin050
  Placement = pos=(164.341,-96.0628,1.65) rot=(0,0,1;0rad)
FEATURE [Part::Feature] Part__Feature051  label="R_0805_2012Metric052"
  shape: bbox 2 x 1.2 x 0.45 mm, 26 faces (baked)
FEATURE [App::Part] R_0805_2012Metric026  label="R_0805_2012Metric053"
  Group = -> [Part__Feature051]
  Origin = -> Origin051
  Placement = pos=(161.8,-79.9592,1.65) rot=(0,0,1;3.14159rad)
FEATURE [Part::Feature] Part__Feature052  label="R_0805_2012Metric054"
  shape: bbox 2 x 1.2 x 0.45 mm, 26 faces (baked)
FEATURE [App::Part] R_0805_2012Metric027  label="R_0805_2012Metric055"
  Group = -> [Part__Feature052]
  Origin = -> Origin052
  Placement = pos=(172.593,-72.9507,1.65) rot=(0,0,-1;1.5708rad)
FEATURE [Part::Feature] Part__Feature053  label="R_0805_2012Metric056"
  shape: bbox 2 x 1.2 x 0.45 mm, 26 faces (baked)
FEATURE [App::Part] R_0805_2012Metric028  label="R_0805_2012Metric057"
  Group = -> [Part__Feature053]
  Origin = -> Origin053
  Placement = pos=(185.623,-80.6215,1.65) rot=(0,0,1;1.5708rad)
FEATURE [Part::Feature] Part__Feature054  label="R_0805_2012Metric058"
  shape: bbox 2 x 1.2 x 0.45 mm, 26 faces (baked)
FEATURE [App::Part] R_0805_2012Metric029  label="R_0805_2012Metric059"
  Group = -> [Part__Feature054]
  Origin = -> Origin054
  Placement = pos=(165.349,-82.648,1.65) rot=(0,0,-1;1.5708rad)
FEATURE [Part::Feature] Part__Feature055  label="C_1206_3216Metric018"
  shape: bbox 3.2 x 1.6 x 1.6 mm, 28 faces (baked)
FEATURE [App::Part] C_1206_3216Metric009  label="C_1206_3216Metric019"
  Group = -> [Part__Feature055]
  Origin = -> Origin055
  Placement = pos=(165.43,-72.2648,1.65) rot=(0,0,-1;1.5708rad)
FEATURE [Part::Feature] Part__Feature056  label="SOT_23_006"
  shape: bbox 2.8 x 2.9 x 1.55 mm, 109 faces (baked)
FEATURE [App::Part] SOT_23_5001  label="SOT-23-006"
  Group = -> [Part__Feature056]
  Origin = -> Origin056
  Placement = pos=(180.462,-71.6178,1.65) rot=(0,0,1;3.14159rad)
FEATURE [Part::Feature] Part__Feature057  label="SW_PUSH_6mm006"
  shape: bbox 7.174 x 6 x 7.8 mm, 105 faces (baked)
FEATURE [App::Part] SW_PUSH_6mm003  label="SW_PUSH_6mm007"
  Group = -> [Part__Feature057]
  Origin = -> Origin057
  Placement = pos=(192.345,-78.9365,1.65) rot=(0,0,1;1.5708rad)
FEATURE [Part::Feature] Part__Feature058  label="C_1206_3216Metric020"
  shape: bbox 3.2 x 1.6 x 1.6 mm, 28 faces (baked)
FEATURE [App::Part] C_1206_3216Metric010  label="C_1206_3216Metric021"
  Group = -> [Part__Feature058]
  Origin = -> Origin058
  Placement = pos=(181.204,-90.6798,1.65) rot=(0,0,-1;1.5708rad)
FEATURE [Part::Feature] Part__Feature059  label="CP_Elec_63x060"
  shape: bbox 8.606 x 8.603 x 5.8 mm, 41 faces (baked)
FEATURE [App::Part] CP_Elec_6_3x5_8002  label="CP_Elec_6.3x5.010"
  Group = -> [Part__Feature059]
  Origin = -> Origin059
  Placement = pos=(158.275,-86.5378,1.65) rot=(0,0,1;3.14159rad)
FEATURE [Part::Feature] Part__Feature060  label="R_0805_2012Metric060"
  shape: bbox 2 x 1.2 x 0.45 mm, 26 faces (baked)
FEATURE [App::Part] R_0805_2012Metric030  label="R_0805_2012Metric061"
  Group = -> [Part__Feature060]
  Origin = -> Origin060
  Placement = pos=(185.344,-76.8331,1.65) rot=(0,0,-1;1.5708rad)
FEATURE [Part::Feature] Part__Feature061  label="C_1206_3216Metric022"
  shape: bbox 3.2 x 1.6 x 1.6 mm, 28 faces (baked)
FEATURE [App::Part] C_1206_3216Metric011  label="C_1206_3216Metric023"
  Group = -> [Part__Feature061]
  Origin = -> Origin061
  Placement = pos=(159.029,-92.6846,1.65) rot=(0,0,1;0rad)
FEATURE [Part::Feature] Part__Feature062  label="R_0805_2012Metric062"
  shape: bbox 2 x 1.2 x 0.45 mm, 26 faces (baked)
FEATURE [App::Part] R_0805_2012Metric031  label="R_0805_2012Metric063"
  Group = -> [Part__Feature062]
  Origin = -> Origin062
  Placement = pos=(201.168,-83.0053,1.65) rot=(0,0,1;1.5708rad)
FEATURE [Part::Feature] Part__Feature063  label="C_1206_3216Metric024"
  shape: bbox 3.2 x 1.6 x 1.6 mm, 28 faces (baked)
FEATURE [App::Part] C_1206_3216Metric012  label="C_1206_3216Metric025"
  Group = -> [Part__Feature063]
  Origin = -> Origin063
  Placement = pos=(165.405,-78.4352,1.65) rot=(0,0,-1;1.5708rad)
FEATURE [Part::Feature] Part__Feature064  label="R_0805_2012Metric064"
  shape: bbox 2 x 1.2 x 0.45 mm, 26 faces (baked)
FEATURE [App::Part] R_0805_2012Metric032  label="R_0805_2012Metric065"
  Group = -> [Part__Feature064]
  Origin = -> Origin064
  Placement = pos=(186.534,-107.436,1.65) rot=(0,0,1;3.14159rad)
FEATURE [Part::Feature] Part__Feature065  label="C_1206_3216Metric026"
  shape: bbox 3.2 x 1.6 x 1.6 mm, 28 faces (baked)
FEATURE [App::Part] C_1206_3216Metric013  label="C_1206_3216Metric027"
  Group = -> [Part__Feature065]
  Origin = -> Origin065
  Placement = pos=(153.543,-75.487,1.65) rot=(0,0,-1;1.5708rad)
FEATURE [Part::Feature] Part__Feature066  label="CP_Elec_63x061"
  shape: bbox 8.606 x 8.603 x 5.8 mm, 41 faces (baked)
FEATURE [App::Part] CP_Elec_6_3x5_8003  label="CP_Elec_6.3x5.011"
  Group = -> [Part__Feature066]
  Origin = -> Origin066
  Placement = pos=(176.497,-95.8596,1.65) rot=(0,0,1;1.5708rad)
FEATURE [Part::Feature] Part__Feature067  label="C_1206_3216Metric028"
  shape: bbox 3.2 x 1.6 x 1.6 mm, 28 faces (baked)
FEATURE [App::Part] C_1206_3216Metric014  label="C_1206_3216Metric029"
  Group = -> [Part__Feature067]
  Origin = -> Origin067
  Placement = pos=(188.39,-71.12,1.65) rot=(0,0,1;0rad)
FEATURE [Part::Feature] Part__Feature068  label="SOIC_20W_75x128mm_P127mm001"
  shape: bbox 10.3 x 12.8 x 2.75 mm, 336 faces (baked)
FEATURE [App::Part] SOIC_20W_7_5x12_8mm_P1_27mm001  label="SOIC-20W_7.5x12.8mm_P1.27mm001"
  Group = -> [Part__Feature068]
  Origin = -> Origin068
  Placement = pos=(174.668,-81.4015,1.65) rot=(0,0,1;0rad)
FEATURE [Part::Feature] Part__Feature069  label="R_0805_2012Metric066"
  shape: bbox 2 x 1.2 x 0.45 mm, 26 faces (baked)
FEATURE [App::Part] R_0805_2012Metric033  label="R_0805_2012Metric067"
  Group = -> [Part__Feature069]
  Origin = -> Origin069
  Placement = pos=(174.322,-102.464,1.65) rot=(0,0,1;3.14159rad)
FEATURE [Part::Feature] Part__Feature070  label="C_1206_3216Metric030"
  shape: bbox 3.2 x 1.6 x 1.6 mm, 28 faces (baked)
FEATURE [App::Part] C_1206_3216Metric015  label="C_1206_3216Metric031"
  Group = -> [Part__Feature070]
  Origin = -> Origin070
  Placement = pos=(175.184,-71.931,1.65) rot=(0,0,1;1.5708rad)
FEATURE [Part::Feature] Part__Feature071  label="R_0805_2012Metric068"
  shape: bbox 2 x 1.2 x 0.45 mm, 26 faces (baked)
FEATURE [App::Part] R_0805_2012Metric034  label="R_0805_2012Metric069"
  Group = -> [Part__Feature071]
  Origin = -> Origin071
  Placement = pos=(204.82,-83.1541,1.65) rot=(0,0,1;3.14159rad)
FEATURE [Part::Feature] Part__Feature072  label="UCHET_PLUS_1_8_PCB"
  shape: bbox 70 x 44 x 1.6 mm, 22 faces (baked)
FEATURE [App::Part] UCHET_PLUS_1_8_1001  label="UCHET_PLUS_1_8 002"
  Group = -> [SW_PUSH_6mm002,R_0805_2012Metric017,R_1206_3216Metric,R_0805_2012Metric018,R_0805_2012Metric019,LED_D3_0mm_IRGrey001,R_0805_2012Metric020,C_1206_3216Metric008,R_0805_2012Metric021,R_0805_2012Metric022,R_0805_2012Metric023,R_0805_2012Metric024,ESP_12E001,R_0805_2012Metric025,L_1210_3225Metric001,R_0805_2012Metric026,R_0805_2012Metric027,R_0805_2012Metric028,R_0805_2012Metric029,+18 more]
  Origin = -> Origin072
  Placement = pos=(112,-140.5,74) rot=(0.707107,0.707107,0;3.14159rad)
FEATURE [Part::FeaturePython] Tube008  # WARN: FeaturePython — macro-defined, semantics opaque (R4)
  AttacherType = Attacher::AttachEngine3D
  Height = 31
  InnerRadius = 1.4
  OuterRadius = 2.5
  Placement = pos=(-2,17,64.5) rot=(0,0,1;0rad)
FEATURE [Part::FeaturePython] Tube009  # WARN: FeaturePython — macro-defined, semantics opaque (R4)
  AttacherType = Attacher::AttachEngine3D
  Height = 31
  InnerRadius = 1.4
  OuterRadius = 2.5
  Placement = pos=(46.5,17,64.5) rot=(0,0,1;0rad)
FEATURE [Part::FeaturePython] Tube010  # WARN: FeaturePython — macro-defined, semantics opaque (R4)
  AttacherType = Attacher::AttachEngine3D
  Height = 31
  InnerRadius = 1.4
  OuterRadius = 2.5
  Placement = pos=(46.5,54,64.5) rot=(0,0,1;0rad)
FEATURE [Part::FeaturePython] Tube011  # WARN: FeaturePython — macro-defined, semantics opaque (R4)
  AttacherType = Attacher::AttachEngine3D
  Height = 31
  InnerRadius = 1.4
  OuterRadius = 2.5
  Placement = pos=(-2,54,64.5) rot=(0,0,1;0rad)
FEATURE [Part::MultiFuse] Fusion025
  Shapes = -> [Tube008,Tube009,Tube010,Tube011]
FEATURE [Part::FeaturePython] Tube012  # WARN: FeaturePython — macro-defined, semantics opaque (R4)
  AttacherType = Attacher::AttachEngine3D
  Height = 3
  InnerRadius = 1.4
  OuterRadius = 3
  Placement = pos=(-2,17,61.5) rot=(0,0,1;0rad)
FEATURE [Part::FeaturePython] Tube013  # WARN: FeaturePython — macro-defined, semantics opaque (R4)
  AttacherType = Attacher::AttachEngine3D
  Height = 3
  InnerRadius = 1.4
  OuterRadius = 3
  Placement = pos=(-2,54,61.5) rot=(0,0,1;0rad)
FEATURE [Part::FeaturePython] Tube014  # WARN: FeaturePython — macro-defined, semantics opaque (R4)
  AttacherType = Attacher::AttachEngine3D
  Height = 3
  InnerRadius = 1.4
  OuterRadius = 3
  Placement = pos=(46.5,17,61.5) rot=(0,0,1;0rad)
FEATURE [Part::FeaturePython] Tube015  # WARN: FeaturePython — macro-defined, semantics opaque (R4)
  AttacherType = Attacher::AttachEngine3D
  Height = 3
  InnerRadius = 1.4
  OuterRadius = 3
  Placement = pos=(46.5,54,61.5) rot=(0,0,1;0rad)
FEATURE [Part::MultiFuse] Fusion026
  Shapes = -> [Tube012,Tube013,Tube014,Tube015]
FEATURE [Part::MultiFuse] Fusion027
  Shapes = -> [Cut040,Fusion026]
FEATURE [Part::MultiFuse] Fusion028
  Shapes = -> [Fusion023,Fusion025]
FEATURE [Part::Cylinder] Cylinder027  label="Цилиндр027"
  Angle = 360
  AttacherType = Attacher::AttachEngine3D
  FirstAngle = 0
  Height = 10
  Radius = 1.5
  SecondAngle = 0
FEATURE [Part::Cylinder] Cylinder028  label="Цилиндр028"
  Angle = 360
  AttacherType = Attacher::AttachEngine3D
  FirstAngle = 0
  Height = 1.8
  Placement = pos=(0,0,-2) rot=(0,0,1;0rad)
  Radius = 2.5
  SecondAngle = 0
FEATURE [Part::MultiFuse] Fusion029
  Placement = pos=(-2,17,63.5) rot=(0,0,1;0rad)
  Shapes = -> [Cylinder027,Cylinder028]
FEATURE [Part::Cylinder] Cylinder029  label="Цилиндр029"
  Angle = 360
  AttacherType = Attacher::AttachEngine3D
  FirstAngle = 0
  Height = 10
  Radius = 1.5
  SecondAngle = 0
FEATURE [Part::Cylinder] Cylinder030  label="Цилиндр030"
  Angle = 360
  AttacherType = Attacher::AttachEngine3D
  FirstAngle = 0
  Height = 1.8
  Placement = pos=(0,0,-2) rot=(0,0,1;0rad)
  Radius = 2.5
  SecondAngle = 0
FEATURE [Part::MultiFuse] Fusion030
  Placement = pos=(-2,54,63.5) rot=(0,0,1;0rad)
  Shapes = -> [Cylinder029,Cylinder030]
FEATURE [Part::Cylinder] Cylinder031  label="Цилиндр031"
  Angle = 360
  AttacherType = Attacher::AttachEngine3D
  FirstAngle = 0
  Height = 10
  Radius = 1.5
  SecondAngle = 0
FEATURE [Part::Cylinder] Cylinder032  label="Цилиндр032"
  Angle = 360
  AttacherType = Attacher::AttachEngine3D
  FirstAngle = 0
  Height = 1.8
  Placement = pos=(0,0,-2) rot=(0,0,1;0rad)
  Radius = 2.5
  SecondAngle = 0
FEATURE [Part::MultiFuse] Fusion031
  Placement = pos=(46.5,54,63.5) rot=(0,0,1;0rad)
  Shapes = -> [Cylinder031,Cylinder032]
FEATURE [Part::Cylinder] Cylinder033  label="Цилиндр033"
  Angle = 360
  AttacherType = Attacher::AttachEngine3D
  FirstAngle = 0
  Height = 10
  Radius = 1.5
  SecondAngle = 0
FEATURE [Part::Cylinder] Cylinder034  label="Цилиндр034"
  Angle = 360
  AttacherType = Attacher::AttachEngine3D
  FirstAngle = 0
  Height = 1.8
  Placement = pos=(0,0,-2) rot=(0,0,1;0rad)
  Radius = 2.5
  SecondAngle = 0
FEATURE [Part::MultiFuse] Fusion032
  Placement = pos=(46.5,17,63.5) rot=(0,0,1;0rad)
  Shapes = -> [Cylinder033,Cylinder034]
FEATURE [Part::MultiFuse] Fusion033
  Shapes = -> [Fusion032,Fusion031,Fusion030,Fusion029]
FEATURE [Part::Cylinder] Cylinder035  label="Цилиндр035"
  Angle = 360
  AttacherType = Attacher::AttachEngine3D
  FirstAngle = 0
  Height = 10
  Radius = 1.5
  SecondAngle = 0
FEATURE [Part::Cylinder] Cylinder036  label="Цилиндр036"
  Angle = 360
  AttacherType = Attacher::AttachEngine3D
  FirstAngle = 0
  Height = 1.8
  Placement = pos=(0,0,-2) rot=(0,0,1;0rad)
  Radius = 2.5
  SecondAngle = 0
FEATURE [Part::Cylinder] Cylinder037  label="Цилиндр037"
  Angle = 360
  AttacherType = Attacher::AttachEngine3D
  FirstAngle = 0
  Height = 10
  Radius = 1.5
  SecondAngle = 0
FEATURE [Part::Cylinder] Cylinder038  label="Цилиндр038"
  Angle = 360
  AttacherType = Attacher::AttachEngine3D
  FirstAngle = 0
  Height = 1.8
  Placement = pos=(0,0,-2) rot=(0,0,1;0rad)
  Radius = 2.5
  SecondAngle = 0
FEATURE [Part::Cylinder] Cylinder039  label="Цилиндр039"
  Angle = 360
  AttacherType = Attacher::AttachEngine3D
  FirstAngle = 0
  Height = 10
  Radius = 1.5
  SecondAngle = 0
FEATURE [Part::Cylinder] Cylinder040  label="Цилиндр040"
  Angle = 360
  AttacherType = Attacher::AttachEngine3D
  FirstAngle = 0
  Height = 1.8
  Placement = pos=(0,0,-2) rot=(0,0,1;0rad)
  Radius = 2.5
  SecondAngle = 0
FEATURE [Part::Cylinder] Cylinder041  label="Цилиндр041"
  Angle = 360
  AttacherType = Attacher::AttachEngine3D
  FirstAngle = 0
  Height = 10
  Radius = 1.5
  SecondAngle = 0
FEATURE [Part::Cylinder] Cylinder042  label="Цилиндр042"
  Angle = 360
  AttacherType = Attacher::AttachEngine3D
  FirstAngle = 0
  Height = 1.8
  Placement = pos=(0,0,-2) rot=(0,0,1;0rad)
  Radius = 2.5
  SecondAngle = 0
FEATURE [Part::MultiFuse] Fusion034
  Placement = pos=(-2,17,63.5) rot=(0,0,1;0rad)
  Shapes = -> [Cylinder035,Cylinder036]
FEATURE [Part::MultiFuse] Fusion035
  Placement = pos=(-2,54,63.5) rot=(0,0,1;0rad)
  Shapes = -> [Cylinder037,Cylinder038]
FEATURE [Part::MultiFuse] Fusion036
  Placement = pos=(46.5,54,63.5) rot=(0,0,1;0rad)
  Shapes = -> [Cylinder039,Cylinder040]
FEATURE [Part::MultiFuse] Fusion037
  Placement = pos=(46.5,17,63.5) rot=(0,0,1;0rad)
  Shapes = -> [Cylinder041,Cylinder042]
FEATURE [Part::MultiFuse] Fusion038
  Placement = pos=(0,0,1) rot=(0,0,1;0rad)
  Shapes = -> [Fusion037,Fusion036,Fusion035,Fusion034]
FEATURE [Part::Cut] Cut042
  Base = -> Fusion027
  Placement = pos=(0,0,-62) rot=(0,0,1;0rad)
  Tool = -> Fusion033
FEATURE [Part::Cut] Cut043
  Base = -> Fusion028
  Tool = -> Fusion038
FEATURE [Part::Cylinder] Cylinder043  label="Цилиндр043"
  Angle = 360
  AttacherType = Attacher::AttachEngine3D
  FirstAngle = 0
  Height = 10
  Radius = 1.5
  SecondAngle = 0
FEATURE [Part::Cylinder] Cylinder044  label="Цилиндр044"
  Angle = 360
  AttacherType = Attacher::AttachEngine3D
  FirstAngle = 0
  Height = 1.8
  Placement = pos=(0,0,-2) rot=(0,0,1;0rad)
  Radius = 2.5
  SecondAngle = 0
FEATURE [Part::Cylinder] Cylinder045  label="Цилиндр045"
  Angle = 360
  AttacherType = Attacher::AttachEngine3D
  FirstAngle = 0
  Height = 10
  Radius = 1.5
  SecondAngle = 0
FEATURE [Part::Cylinder] Cylinder046  label="Цилиндр046"
  Angle = 360
  AttacherType = Attacher::AttachEngine3D
  FirstAngle = 0
  Height = 1.8
  Placement = pos=(0,0,-2) rot=(0,0,1;0rad)
  Radius = 2.5
  SecondAngle = 0
FEATURE [Part::Cylinder] Cylinder047  label="Цилиндр047"
  Angle = 360
  AttacherType = Attacher::AttachEngine3D
  FirstAngle = 0
  Height = 10
  Radius = 1.5
  SecondAngle = 0
FEATURE [Part::Cylinder] Cylinder048  label="Цилиндр048"
  Angle = 360
  AttacherType = Attacher::AttachEngine3D
  FirstAngle = 0
  Height = 1.8
  Placement = pos=(0,0,-2) rot=(0,0,1;0rad)
  Radius = 2.5
  SecondAngle = 0
FEATURE [Part::Cylinder] Cylinder049  label="Цилиндр049"
  Angle = 360
  AttacherType = Attacher::AttachEngine3D
  FirstAngle = 0
  Height = 10
  Radius = 1.5
  SecondAngle = 0
FEATURE [Part::Cylinder] Cylinder050  label="Цилиндр050"
  Angle = 360
  AttacherType = Attacher::AttachEngine3D
  FirstAngle = 0
  Height = 1.8
  Placement = pos=(0,0,-2) rot=(0,0,1;0rad)
  Radius = 2.5
  SecondAngle = 0
FEATURE [Part::MultiFuse] Fusion039
  Placement = pos=(-2,17,63.5) rot=(0,0,1;0rad)
  Shapes = -> [Cylinder043,Cylinder044]
FEATURE [Part::MultiFuse] Fusion040
  Placement = pos=(-2,54,63.5) rot=(0,0,1;0rad)
  Shapes = -> [Cylinder045,Cylinder046]
FEATURE [Part::MultiFuse] Fusion041
  Placement = pos=(46.5,54,63.5) rot=(0,0,1;0rad)
  Shapes = -> [Cylinder047,Cylinder048]
FEATURE [Part::MultiFuse] Fusion042
  Placement = pos=(46.5,17,63.5) rot=(0,0,1;0rad)
  Shapes = -> [Cylinder049,Cylinder050]
FEATURE [Part::MultiFuse] Fusion043
  Placement = pos=(0,0,-89) rot=(0,0,1;0rad)
  Shapes = -> [Fusion042,Fusion041,Fusion040,Fusion039]
FEATURE [Part::Cylinder] Cylinder051  label="Цилиндр051"
  Angle = 360
  AttacherType = Attacher::AttachEngine3D
  FirstAngle = 0
  Height = 7
  Placement = pos=(36.2,63.3,61) rot=(0,0,1;0rad)
  Radius = 1.5
  SecondAngle = 0
FEATURE [Part::Cylinder] Cylinder052  label="Цилиндр052"
  Angle = 360
  AttacherType = Attacher::AttachEngine3D
  FirstAngle = 0
  Height = 7
  Placement = pos=(36.2,54.2,61) rot=(0,0,1;0rad)
  Radius = 1.5
  SecondAngle = 0
FEATURE [Part::MultiFuse] Fusion044
  Placement = pos=(-13.5,-23,32) rot=(0,0,1;0rad)
  Shapes = -> [Cylinder052,Cylinder051]
FEATURE [Part::Cylinder] Cylinder053  label="Цилиндр053"
  Angle = 360
  AttacherType = Attacher::AttachEngine3D
  FirstAngle = 0
  Height = 7
  Placement = pos=(36.2,63.3,61) rot=(0,0,1;0rad)
  Radius = 1.5
  SecondAngle = 0
FEATURE [Part::Cylinder] Cylinder054  label="Цилиндр054"
  Angle = 360
  AttacherType = Attacher::AttachEngine3D
  FirstAngle = 0
  Height = 7
  Placement = pos=(36.2,54.2,61) rot=(0,0,1;0rad)
  Radius = 1.5
  SecondAngle = 0
FEATURE [Part::MultiFuse] Fusion045
  Placement = pos=(-13.5,-23,32) rot=(0,0,1;0rad)
  Shapes = -> [Cylinder054,Cylinder053]
FEATURE [Part::Cut] Cut044
  Base = -> Cut043
  Tool = -> Fusion044
FEATURE [Part::Cut] Cut045
  Base = -> Fusion015
  Placement = pos=(0,0,48) rot=(0,0,1;0rad)
  Tool = -> Fusion045
